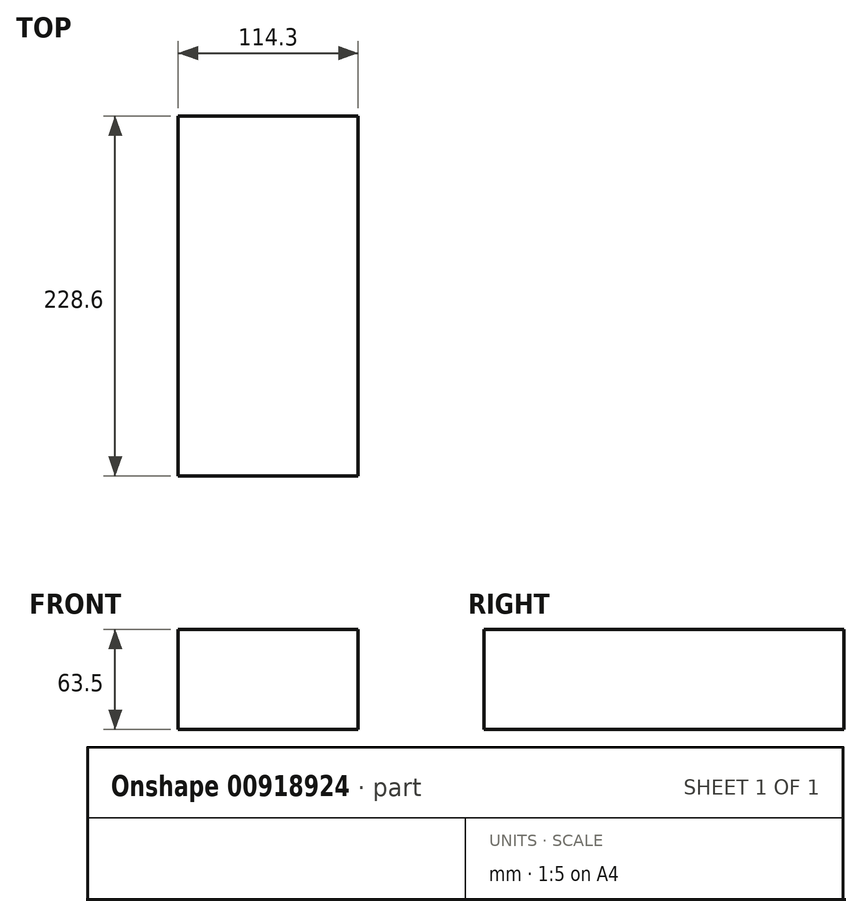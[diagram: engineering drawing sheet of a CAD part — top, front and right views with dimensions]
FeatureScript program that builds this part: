
annotation { "Feature Type Name" : "Feature", "Feature Type Description" : "" }
export const myFeature = defineFeature(function(context is Context, id is Id, definition is map)
    precondition{}
    {
        {
            var Q0;
            Q0=qCreatedBy(makeId("Front.planeOp"),FACE);
            var sketch = newSketch(context, id + "F0", { "sketchPlane" : qUnion([Q0])});
            skLineSegment(sketch, "E0.bottom", {"start": v(-57.15, 0) * mm, "end": v(57.15, 0) * mm});
            skLineSegment(sketch, "E0.top", {"start": v(-57.15, -63.5) * mm, "end": v(57.15, -63.5) * mm});
            skLineSegment(sketch, "E0.left", {"start": v(-57.15, 0) * mm, "end": v(-57.15, -63.5) * mm});
            skLineSegment(sketch, "E0.right", {"start": v(57.15, 0) * mm, "end": v(57.15, -63.5) * mm});
            skSolve(sketch);
        }
        {
            var Q0;
            Q0 = qSketchRegion(id + "F0", true);
            extrude(context, id + "F1", {"entities" : qUnion([Q0]), "depth" : 228.6 * mm, "offsetDistance" : 25.4 * mm});
        }
    });
